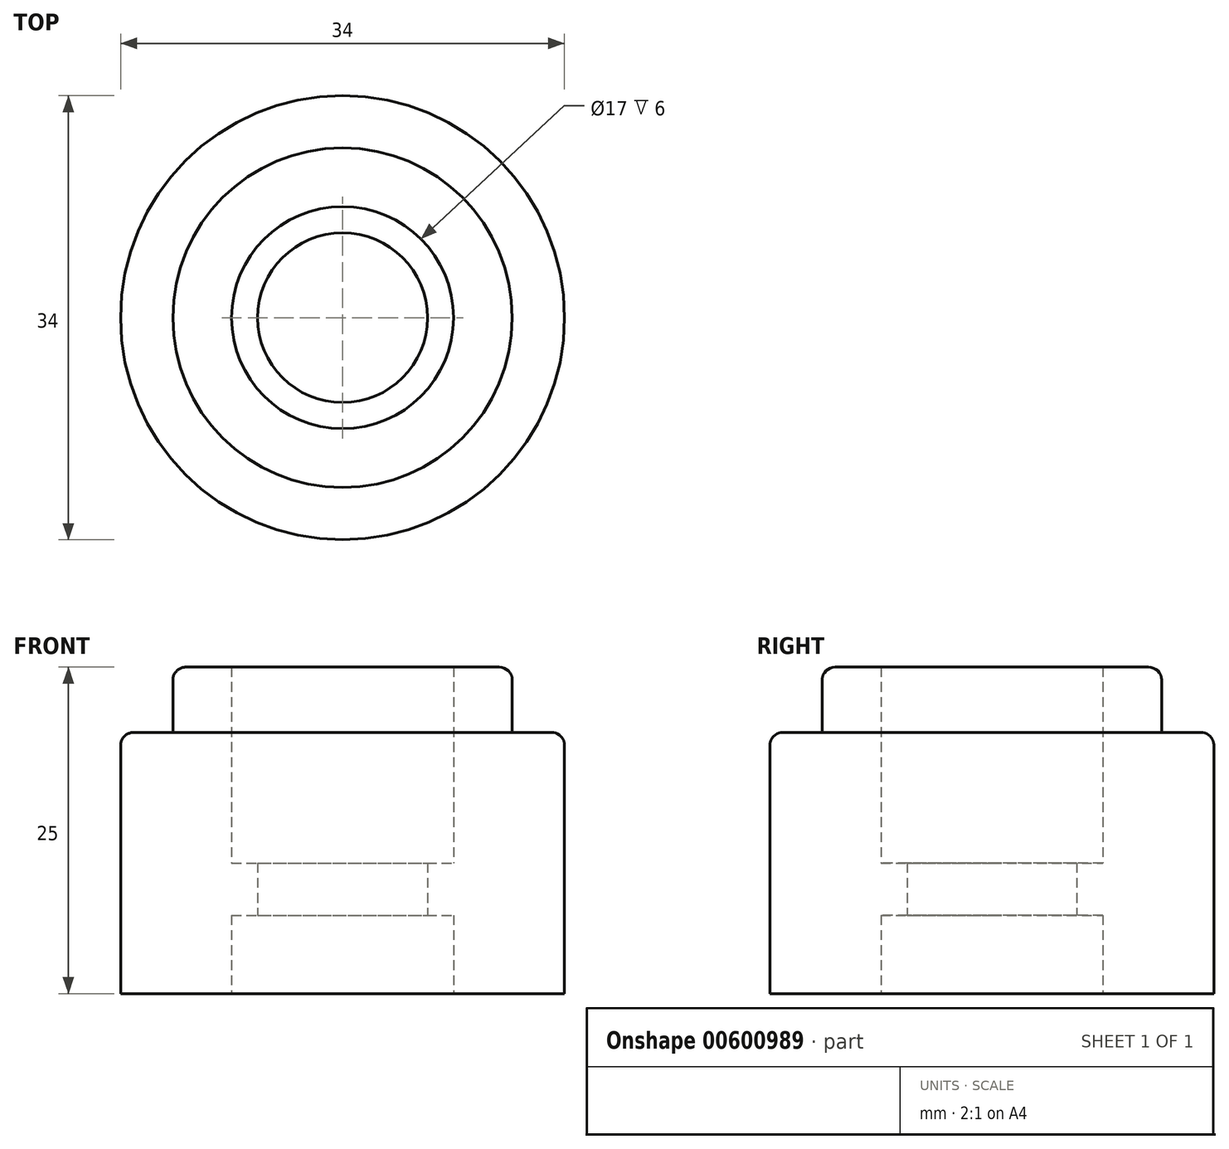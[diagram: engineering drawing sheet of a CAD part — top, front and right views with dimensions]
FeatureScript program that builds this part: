
annotation { "Feature Type Name" : "Feature", "Feature Type Description" : "" }
export const myFeature = defineFeature(function(context is Context, id is Id, definition is map)
    precondition{}
    {
        {
            var Q0;
            Q0=qCreatedBy(makeId("Top.planeOp"),FACE);
            var sketch = newSketch(context, id + "F0", { "sketchPlane" : qUnion([Q0])});
            skCircle(sketch, "E0", {"center": v(0, 0) * mm, "radius": 17 * mm});
            skCircle(sketch, "E1", {"center": v(0, 0) * mm, "radius": 11 * mm});
            skSolve(sketch);
        }
        {
            var Q0;
            Q0=qCreatedBy(makeId("Front.planeOp"),FACE);
            var sketch = newSketch(context, id + "F1", { "sketchPlane" : qUnion([Q0])});
            skLineSegment(sketch, "E2", {"start": v(0, 0) * mm, "end": v(0, 25) * mm});
            skLineSegment(sketch, "E3.0", {"start": v(17, 0) * mm, "end": v(17, 19) * mm});
            skLineSegment(sketch, "E4", {"start": v(8.5, 0) * mm, "end": v(17, 0) * mm});
            skLineSegment(sketch, "E5.0", {"start": v(6.5, 10) * mm, "end": v(8.5, 10) * mm});
            skLineSegment(sketch, "E6", {"start": v(8.5, 25) * mm, "end": v(12, 25) * mm});
            skLineSegment(sketch, "E7.0", {"start": v(13, 20) * mm, "end": v(13, 24) * mm});
            skLineSegment(sketch, "E8.0", {"start": v(13, 20) * mm, "end": v(16, 20) * mm});
            skPoint(sketch, "E9.visualSharp", {"position": v(13, 25) * mm});
            skArc(sketch, "E9.filletArc", {"start": v(13, 24) * mm, "mid": v(12.7, 24.7) * mm, "end": v(12, 25) * mm});
            skPoint(sketch, "E10.visualSharp", {"position": v(17, 20) * mm});
            skArc(sketch, "E10.filletArc", {"start": v(17, 19) * mm, "mid": v(16.7, 19.7) * mm, "end": v(16, 20) * mm});
            skLineSegment(sketch, "E11.0", {"start": v(8.5, 0) * mm, "end": v(8.5, 6) * mm});
            skLineSegment(sketch, "E12.0", {"start": v(6.5, 6) * mm, "end": v(6.5, 10) * mm});
            skLineSegment(sketch, "E13.trimOffspring", {"start": v(8.5, 10) * mm, "end": v(8.5, 25) * mm});
            skLineSegment(sketch, "E14.0", {"start": v(6.5, 6) * mm, "end": v(8.5, 6) * mm});
            skSolve(sketch);
        }
        {
            var Q0;
            Q0 = qSketchRegion(id + "F1", true);
            var Q1;
            Q1=sQuery(id+"F1.wireOp",EDGE,"E2");
            revolve(context, id + "F2", {"entities" : qUnion([Q0]), "axis" : qUnion([Q1]), "revolveType" : RevolveType.FULL});
        }
    });
